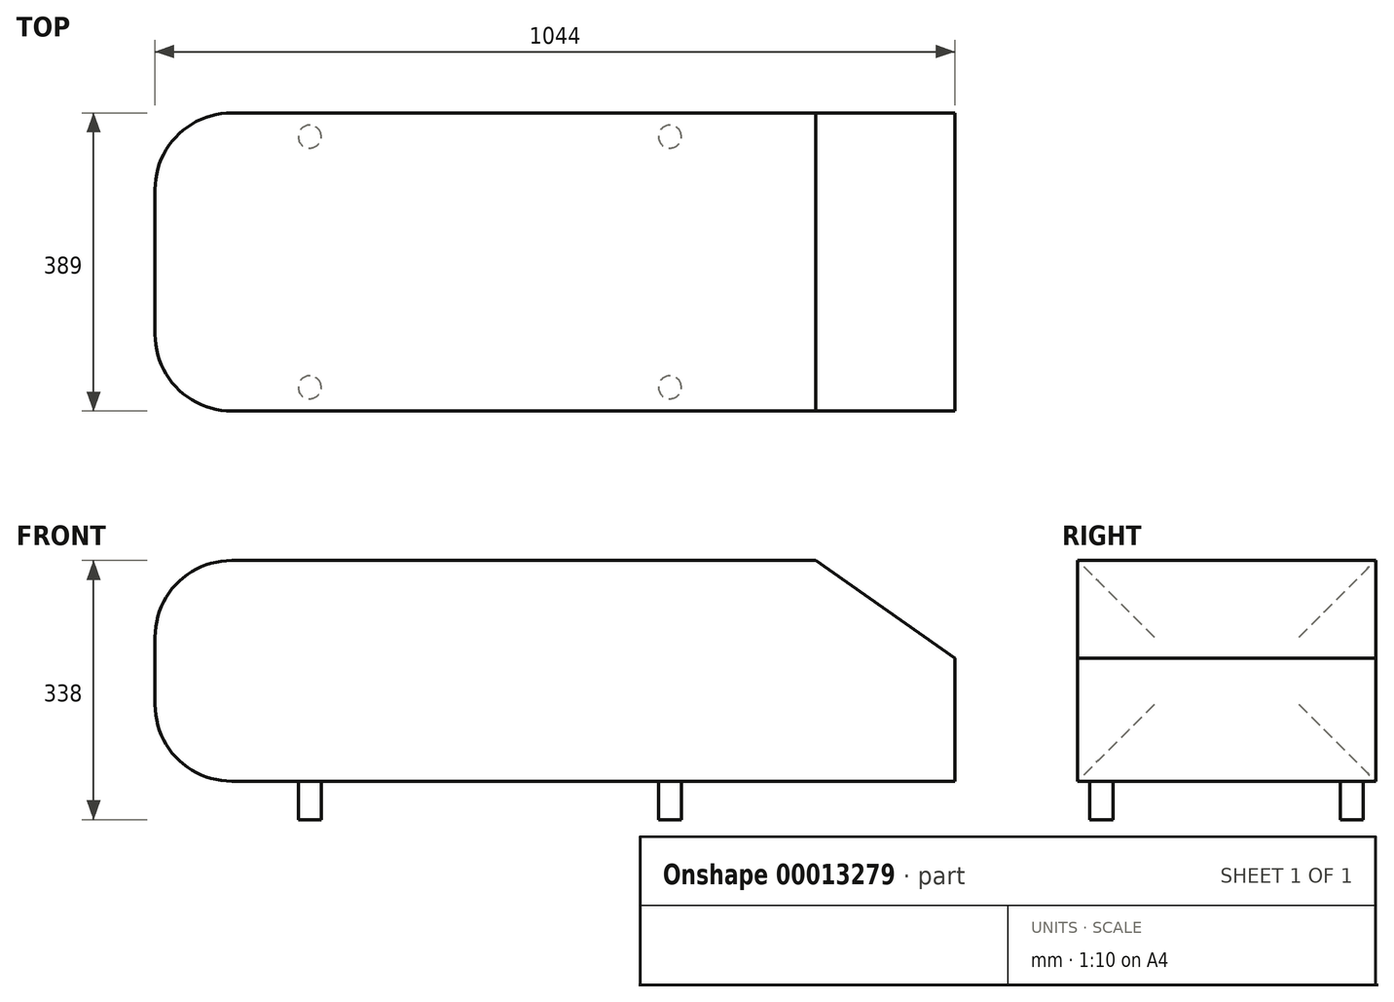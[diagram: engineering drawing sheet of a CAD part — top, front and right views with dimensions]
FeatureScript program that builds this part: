
annotation { "Feature Type Name" : "Feature", "Feature Type Description" : "" }
export const myFeature = defineFeature(function(context is Context, id is Id, definition is map)
    precondition{}
    {
        {
            var Q0;
            Q0=qCreatedBy(makeId("Top.planeOp"),FACE);
            var sketch = newSketch(context, id + "F0", { "sketchPlane" : qUnion([Q0])});
            skLineSegment(sketch, "E0.rect.bottom", {"start": v(-522, 194.5) * mm, "end": v(522, 194.5) * mm});
            skLineSegment(sketch, "E0.rect.top", {"start": v(-522, -194.5) * mm, "end": v(522, -194.5) * mm});
            skLineSegment(sketch, "E0.rect.left", {"start": v(-522, 194.5) * mm, "end": v(-522, -194.5) * mm});
            skLineSegment(sketch, "E0.rect.right", {"start": v(522, 194.5) * mm, "end": v(522, -194.5) * mm});
            skPoint(sketch, "E0.rect.middle", {"position": v(0, 0) * mm});
            skCircle(sketch, "E1", {"center": v(-320, -163.5) * mm, "radius": 15 * mm});
            skLineSegment(sketch, "E2", {"start": v(-522, 0) * mm, "end": v(522, 0) * mm});
            skCircle(sketch, "E3", {"center": v(-320, 163.5) * mm, "radius": 15 * mm});
            skCircle(sketch, "E4", {"center": v(150, 163.5) * mm, "radius": 15 * mm});
            skCircle(sketch, "E5", {"center": v(150, -163.5) * mm, "radius": 15 * mm});
            skSolve(sketch);
        }
        {
            var Q0;
            Q0=makeQuery(id+"F0.imprint","IMPRINT",FACE,{"disambiguationData":[TD([[makeQuery(id+"F0.imprint","IMPRINT",EDGE,{"derivedFrom":sQuery(id+"F0.wireOp",EDGE,"E1")}),1.0]])]});
            var Q1;
            Q1=makeQuery(id+"F0.imprint","IMPRINT",FACE,{"disambiguationData":[TD([[makeQuery(id+"F0.imprint","IMPRINT",EDGE,{"derivedFrom":sQuery(id+"F0.wireOp",EDGE,"E5")}),1.0]])]});
            var Q2;
            Q2=makeQuery(id+"F0.imprint","IMPRINT",FACE,{"disambiguationData":[TD([[makeQuery(id+"F0.imprint","IMPRINT",EDGE,{"derivedFrom":sQuery(id+"F0.wireOp",EDGE,"E4")}),1.0]])]});
            var Q3;
            Q3=makeQuery(id+"F0.imprint","IMPRINT",FACE,{"disambiguationData":[TD([[makeQuery(id+"F0.imprint","IMPRINT",EDGE,{"derivedFrom":sQuery(id+"F0.wireOp",EDGE,"E3")}),1.0]])]});
            extrude(context, id + "F1", {"entities" : qUnion([Q0, Q1, Q2, Q3]), "oppositeDirection" : true, "depth" : 50 * mm});
        }
        {
            var Q0;
            {var subQ2=sQuery(id+"F0.wireOp",EDGE,"E0.rect.bottom");Q0=makeQuery(id+"F0.imprint","IMPRINT",FACE,{"disambiguationData":[TD([[makeQuery(id+"F0.imprint","IMPRINT",EDGE,{"derivedFrom":subQ2}),-1.0]])]});}
            var Q1;
            {var subQ2=sQuery(id+"F0.wireOp",EDGE,"E0.rect.top");Q1=makeQuery(id+"F0.imprint","IMPRINT",FACE,{"disambiguationData":[TD([[makeQuery(id+"F0.imprint","IMPRINT",EDGE,{"derivedFrom":subQ2}),1.0]])]});}
            var Q2;
            Q2=makeQuery(id+"F0.imprint","IMPRINT",FACE,{"disambiguationData":[TD([[makeQuery(id+"F0.imprint","IMPRINT",EDGE,{"derivedFrom":sQuery(id+"F0.wireOp",EDGE,"E4")}),1.0]])]});
            var Q3;
            Q3=makeQuery(id+"F0.imprint","IMPRINT",FACE,{"disambiguationData":[TD([[makeQuery(id+"F0.imprint","IMPRINT",EDGE,{"derivedFrom":sQuery(id+"F0.wireOp",EDGE,"E3")}),1.0]])]});
            var Q4;
            Q4=makeQuery(id+"F0.imprint","IMPRINT",FACE,{"disambiguationData":[TD([[makeQuery(id+"F0.imprint","IMPRINT",EDGE,{"derivedFrom":sQuery(id+"F0.wireOp",EDGE,"E1")}),1.0]])]});
            var Q5;
            Q5=makeQuery(id+"F0.imprint","IMPRINT",FACE,{"disambiguationData":[TD([[makeQuery(id+"F0.imprint","IMPRINT",EDGE,{"derivedFrom":sQuery(id+"F0.wireOp",EDGE,"E5")}),1.0]])]});
            extrude(context, id + "F2", {"entities" : qUnion([Q0, Q1, Q2, Q3, Q4, Q5]), "depth" : 288 * mm});
        }
        {
            var Q0;
            Q0=makeQuery(id+"F2.opExtrude","CAP_EDGE",EDGE,{"disambiguationData":[OSD([sQuery(id+"F0.wireOp",EDGE,"E0.rect.left")])],"isStart":false});
            var Q1;
            Q1=makeQuery(id+"F2.opExtrude","CAP_EDGE",EDGE,{"disambiguationData":[OSD([sQuery(id+"F0.wireOp",EDGE,"E0.rect.left")])],"isStart":true});
            var Q2;
            Q2=makeQuery(id+"F2.opExtrude","SWEPT_EDGE",EDGE,{"disambiguationData":[OSD([sQuery(id+"F0.wireOp",EDGE,"E0.rect.top"),sQuery(id+"F0.wireOp",EDGE,"E0.rect.left")])]});
            var Q3;
            Q3=makeQuery(id+"F2.opExtrude","SWEPT_EDGE",EDGE,{"disambiguationData":[OSD([sQuery(id+"F0.wireOp",EDGE,"E0.rect.bottom"),sQuery(id+"F0.wireOp",EDGE,"E0.rect.left")])]});
            fillet(context, id + "F3", {"entities" : qUnion([Q0, Q1, Q2, Q3]), "radius" : 100 * mm, "tangentPropagation" : true, "allowEdgeOverflow" : false});
        }
        {
            var Q0;
            Q0=makeQuery(id+"F2.opExtrude","SWEPT_FACE",FACE,{"disambiguationData":[OSD([sQuery(id+"F0.wireOp",EDGE,"E0.rect.top")])]});
            var sketch = newSketch(context, id + "F4", { "sketchPlane" : qUnion([Q0])});
            skLineSegment(sketch, "E6", {"start": v(340.15, 288) * mm, "end": v(522, 160.67) * mm});
            skSolve(sketch);
        }
        {
            var Q0;
            Q0=qSketchRegion(id+"F4",true);
            var Q1;
            {var subQ2=sQuery(id+"F4.wireOp",EDGE,"E6");Q1=makeQuery(id+"F4.imprint","IMPRINT",FACE,{"disambiguationData":[TD([[makeQuery(id+"F4.imprint","IMPRINT",EDGE,{"derivedFrom":subQ2}),1.0]])]});}
            extrude(context, id + "F5", {"entities" : qUnion([Q0, Q1]), "operationType" : NewBodyOperationType.REMOVE, "endBound" : BoundingType.THROUGH_ALL, "oppositeDirection" : true, "depth" : 25 * mm});
        }
    });
